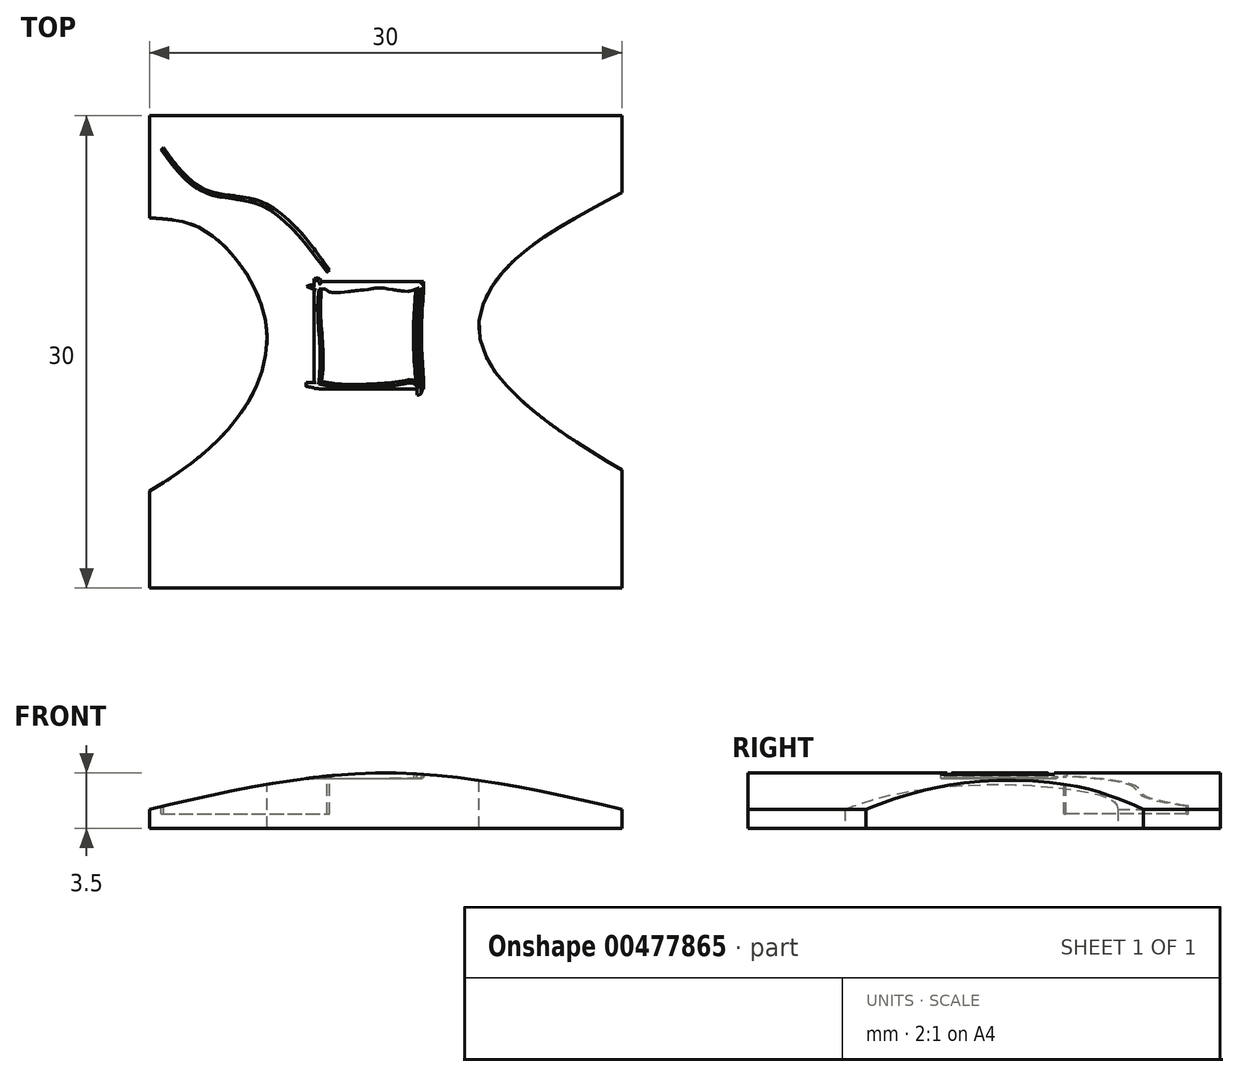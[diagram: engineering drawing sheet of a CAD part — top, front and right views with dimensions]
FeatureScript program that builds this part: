
annotation { "Feature Type Name" : "Feature", "Feature Type Description" : "" }
export const myFeature = defineFeature(function(context is Context, id is Id, definition is map)
    precondition{}
    {
        {
            var Q0;
            Q0=qCreatedBy(makeId("Front.planeOp"),FACE);
            var sketch = newSketch(context, id + "F0", { "sketchPlane" : qUnion([Q0])});
            skLineSegment(sketch, "E0.bottom", {"start": v(0, 0) * mm, "end": v(30, 0) * mm});
            skLineSegment(sketch, "E0.left", {"start": v(0, 0) * mm, "end": v(0, 1.2) * mm});
            skLineSegment(sketch, "E0.right", {"start": v(30, 0) * mm, "end": v(30, 1.2) * mm});
            skLineSegment(sketch, "E1", {"start": v(15, 9.17) * mm, "end": v(15, -5.56) * mm, "construction": true});
            skFitSpline(sketch, "E2", {"points": [v(0, 1.2) * mm, v(15, 3.5) * mm, v(30, 1.2) * mm], "startDerivative": vector(30, 6.9) * mm, "endDerivative": vector(30, -6.9) * mm});
            skPoint(sketch, "E3.orphan", {"position": v(0, 3.5) * mm});
            skPoint(sketch, "E4.orphan", {"position": v(30, 3.5) * mm});
            skSolve(sketch);
        }
        {
            var Q0;
            Q0 = qSketchRegion(id + "F0", true);
            extrude(context, id + "F1", {"entities" : qUnion([Q0]), "depth" : 30 * mm});
        }
        {
            var Q0;
            Q0=makeQuery(id+"F1.opExtrude","SWEPT_FACE",FACE,{"disambiguationData":[OSD([sQuery(id+"F0.wireOp",EDGE,"E0.bottom")])]});
            var sketch = newSketch(context, id + "F2", { "sketchPlane" : qUnion([Q0])});
            skFitSpline(sketch, "E5", {"points": [v(30, 4.87) * mm, v(23.08, 9.25) * mm, v(21, 14.25) * mm, v(30, 22.5) * mm], "startDerivative": vector(-22.26, 12.4) * mm, "endDerivative": vector(35.6, 20.65) * mm});
            skLineSegment(sketch, "E6", {"start": v(30, 4.87) * mm, "end": v(30, 22.5) * mm});
            skFitSpline(sketch, "E7", {"points": [v(0, 6.5) * mm, v(4, 7.62) * mm, v(7, 11.71) * mm, v(7, 16.65) * mm, v(0, 23.84) * mm], "startDerivative": vector(27.81, 1.2) * mm, "endDerivative": vector(-36.4, 21.33) * mm});
            skLineSegment(sketch, "E8", {"start": v(0, 6.5) * mm, "end": v(0, 23.84) * mm});
            skSolve(sketch);
        }
        {
            var Q0;
            Q0 = qSketchRegion(id + "F2", true);
            extrude(context, id + "F3", {"entities" : qUnion([Q0]), "operationType" : NewBodyOperationType.REMOVE, "oppositeDirection" : true, "depth" : 25 * mm});
        }
        {
            var Q0;
            Q0=qCreatedBy(makeId("Top.planeOp"),FACE);
            cPlane(context, id + "F4", {"entities" : qUnion([Q0]), "cplaneType" : CPlaneType.OFFSET, "offset" : 3.5 * mm, "width" : 150 * mm, "height" : 150 * mm});
        }
        {
            var Q0;
            Q0=qCreatedBy(id+"F4.planeOp",FACE);
            var sketch = newSketch(context, id + "F5", { "sketchPlane" : qUnion([Q0])});
            skLineSegment(sketch, "E9.bottom", {"start": v(10.94, -10.52) * mm, "end": v(17.41, -10.52) * mm});
            skLineSegment(sketch, "E9.top", {"start": v(10.44, -17.37) * mm, "end": v(16.99, -17.37) * mm});
            skLineSegment(sketch, "E9.left", {"start": v(10.44, -10.52) * mm, "end": v(10.44, -10.67) * mm});
            skLineSegment(sketch, "E9.right", {"start": v(17.41, -10.52) * mm, "end": v(17.41, -11.02) * mm});
            skLineSegment(sketch, "E10.bottom", {"start": v(10.94, -11.02) * mm, "end": v(11.18, -11.02) * mm});
            skLineSegment(sketch, "E11", {"start": v(10.44, -11.02) * mm, "end": v(9.56, -10.7) * mm});
            skPoint(sketch, "E11.endSnap0", {"position": v(9.56, -11.02) * mm});
            skLineSegment(sketch, "E12", {"start": v(9.56, -10.7) * mm, "end": v(10.44, -10.67) * mm});
            skPoint(sketch, "E13.trimOffspring.end.orphan", {"position": v(8.2, -11.02) * mm});
            skLineSegment(sketch, "E14.trimOffspring", {"start": v(10.44, -11.02) * mm, "end": v(10.44, -16.93) * mm});
            skLineSegment(sketch, "E15", {"start": v(10.44, -10.52) * mm, "end": v(10.44, -10.36) * mm});
            skFitSpline(sketch, "E16", {"points": [v(10.44, -10.36) * mm, v(10.67, -10.31) * mm, v(10.87, -10.4) * mm, v(10.94, -10.52) * mm], "startDerivative": vector(0.62, 0.22) * mm, "endDerivative": vector(0.17, -0.43) * mm});
            skLineSegment(sketch, "E17", {"start": v(9.65, -16.93) * mm, "end": v(10.44, -16.93) * mm});
            skLineSegment(sketch, "E18", {"start": v(10.44, -17.27) * mm, "end": v(9.42, -17.1) * mm});
            skLineSegment(sketch, "E19", {"start": v(9.42, -17.1) * mm, "end": v(9.65, -16.93) * mm});
            skLineSegment(sketch, "E20.trimOffspring", {"start": v(10.44, -17.27) * mm, "end": v(10.44, -17.37) * mm});
            skLineSegment(sketch, "E21", {"start": v(16.99, -17.37) * mm, "end": v(16.99, -17.75) * mm});
            skLineSegment(sketch, "E22", {"start": v(17.33, -17.37) * mm, "end": v(17.31, -17.48) * mm});
            skFitSpline(sketch, "E23", {"points": [v(16.99, -17.75) * mm, v(17.2, -17.7) * mm, v(17.31, -17.48) * mm], "startDerivative": vector(0.47, 0.05) * mm, "endDerivative": vector(0.18, 0.5) * mm});
            skLineSegment(sketch, "E24.trimOffspring", {"start": v(17.33, -17.37) * mm, "end": v(17.41, -17.37) * mm});
            skFitSpline(sketch, "E25", {"points": [v(11.18, -11.02) * mm, v(11.25, -11.12) * mm, v(11.88, -11.24) * mm, v(12.9, -11.14) * mm, v(13.92, -11.02) * mm, v(14.71, -10.94) * mm, v(16.36, -11.15) * mm, v(16.91, -11.02) * mm], "startDerivative": vector(0.68, -1.78) * mm, "endDerivative": vector(3.6, 1.6) * mm});
            skFitSpline(sketch, "E26", {"points": [v(16.91, -11.02) * mm, v(16.76, -14.23) * mm, v(16.91, -16.87) * mm], "startDerivative": vector(-0.45, -6.26) * mm, "endDerivative": vector(0.47, -5.42) * mm});
            skFitSpline(sketch, "E27", {"points": [v(17.41, -11.02) * mm, v(17.27, -13.72) * mm, v(17.41, -16.87) * mm], "startDerivative": vector(-0.43, -5.5) * mm, "endDerivative": vector(0.42, -6.19) * mm});
            skLineSegment(sketch, "E28.trimOffspring", {"start": v(17.41, -16.87) * mm, "end": v(17.41, -17.37) * mm});
            skFitSpline(sketch, "E29", {"points": [v(10.94, -16.87) * mm, v(11.93, -17.03) * mm, v(14, -17.04) * mm, v(15.92, -16.87) * mm, v(16.66, -16.77) * mm, v(16.91, -16.87) * mm], "startDerivative": vector(4.68, -0.99) * mm, "endDerivative": vector(2.25, -1.31) * mm});
            skFitSpline(sketch, "E30", {"points": [v(10.94, -11.02) * mm, v(10.86, -12.07) * mm, v(11.03, -15.52) * mm, v(10.94, -16.87) * mm], "startDerivative": vector(-0.5, -3.3) * mm, "endDerivative": vector(-0.51, -3.86) * mm});
            skSolve(sketch);
        }
        {
            var Q0;
            Q0 = qSketchRegion(id + "F5", true);
            extrude(context, id + "F6", {"entities" : qUnion([Q0]), "operationType" : NewBodyOperationType.REMOVE, "oppositeDirection" : true, "depth" : .35 * mm});
        }
        {
            var Q0;
            Q0=makeQuery(id+"F6.boolean.opBoolean","COPY",EDGE,{"derivedFrom":makeQuery(id+"F6.opExtrude","CAP_EDGE",EDGE,{"disambiguationData":[OSD([sQuery(id+"F5.wireOp",EDGE,"E9.bottom")])],"isStart":false})});
            var Q1;
            Q1=makeQuery(id+"F6.boolean.opBoolean","COPY",EDGE,{"derivedFrom":makeQuery(id+"F6.opExtrude","CAP_EDGE",EDGE,{"disambiguationData":[OSD([sQuery(id+"F5.wireOp",EDGE,"E27")])],"isStart":false})});
            var Q2;
            Q2=makeQuery(id+"F6.boolean.opBoolean","COPY",EDGE,{"derivedFrom":makeQuery(id+"F6.opExtrude","CAP_EDGE",EDGE,{"disambiguationData":[OSD([sQuery(id+"F5.wireOp",EDGE,"E26")])],"isStart":false})});
            var Q3;
            Q3=makeQuery(id+"F6.boolean.opBoolean","COPY",EDGE,{"derivedFrom":makeQuery(id+"F6.opExtrude","CAP_EDGE",EDGE,{"disambiguationData":[OSD([sQuery(id+"F5.wireOp",EDGE,"E29")])],"isStart":false})});
            var Q4;
            Q4=makeQuery(id+"F6.boolean.opBoolean","COPY",EDGE,{"derivedFrom":makeQuery(id+"F6.opExtrude","CAP_EDGE",EDGE,{"disambiguationData":[OSD([sQuery(id+"F5.wireOp",EDGE,"E9.top")])],"isStart":false})});
            var Q5;
            Q5=makeQuery(id+"F6.boolean.opBoolean","COPY",EDGE,{"derivedFrom":makeQuery(id+"F6.opExtrude","CAP_EDGE",EDGE,{"disambiguationData":[OSD([sQuery(id+"F5.wireOp",EDGE,"E14.trimOffspring")])],"isStart":false})});
            var Q6;
            Q6=makeQuery(id+"F6.boolean.opBoolean","COPY",EDGE,{"derivedFrom":makeQuery(id+"F6.opExtrude","CAP_EDGE",EDGE,{"disambiguationData":[OSD([sQuery(id+"F5.wireOp",EDGE,"E30")])],"isStart":false})});
            var Q7;
            Q7=makeQuery(id+"F6.boolean.opBoolean","COPY",EDGE,{"derivedFrom":makeQuery(id+"F6.opExtrude","CAP_EDGE",EDGE,{"disambiguationData":[OSD([sQuery(id+"F5.wireOp",EDGE,"E12")])],"isStart":false})});
            var Q8;
            Q8=makeQuery(id+"F6.boolean.opBoolean","COPY",EDGE,{"derivedFrom":makeQuery(id+"F6.opExtrude","CAP_EDGE",EDGE,{"disambiguationData":[OSD([sQuery(id+"F5.wireOp",EDGE,"E16")])],"isStart":false})});
            fillet(context, id + "F7", {"entities" : qUnion([Q0, Q1, Q2, Q3, Q4, Q5, Q6, Q7, Q8]), "radius" : .2 * mm, "tangentPropagation" : true, "allowEdgeOverflow" : false});
        }
        {
            var Q0;
            Q0=qCreatedBy(id+"F4.planeOp",FACE);
            var sketch = newSketch(context, id + "F8", { "sketchPlane" : qUnion([Q0])});
            skFitSpline(sketch, "E31", {"points": [v(0.72, -2.16) * mm, v(3.5, -4.88) * mm, v(7.13, -5.71) * mm, v(11.28, -9.92) * mm], "startDerivative": vector(8.08, -10.85) * mm, "endDerivative": vector(10.28, -13.83) * mm});
            skFitSpline(sketch, "E32.0", {"points": [v(0.88, -2.04) * mm, v(1.22, -2.49) * mm, v(1.72, -3.16) * mm, v(2.43, -3.92) * mm, v(2.99, -4.39) * mm, v(3.58, -4.73) * mm, v(4.24, -4.92) * mm, v(4.97, -5.03) * mm, v(5.74, -5.13) * mm, v(6.53, -5.28) * mm, v(7.32, -5.55) * mm, v(8.08, -6) * mm, v(9.03, -6.8) * mm, v(10.15, -8.07) * mm, v(11, -9.23) * mm, v(11.44, -9.8) * mm]});
            skLineSegment(sketch, "E33", {"start": v(0.72, -2.16) * mm, "end": v(0.88, -2.04) * mm});
            skLineSegment(sketch, "E34", {"start": v(11.28, -9.92) * mm, "end": v(11.44, -9.8) * mm});
            skSolve(sketch);
        }
        {
            var Q0;
            Q0 = qSketchRegion(id + "F8", true);
            extrude(context, id + "F9", {"entities" : qUnion([Q0]), "operationType" : NewBodyOperationType.REMOVE, "oppositeDirection" : true, "depth" : 2.6 * mm});
        }
    });
